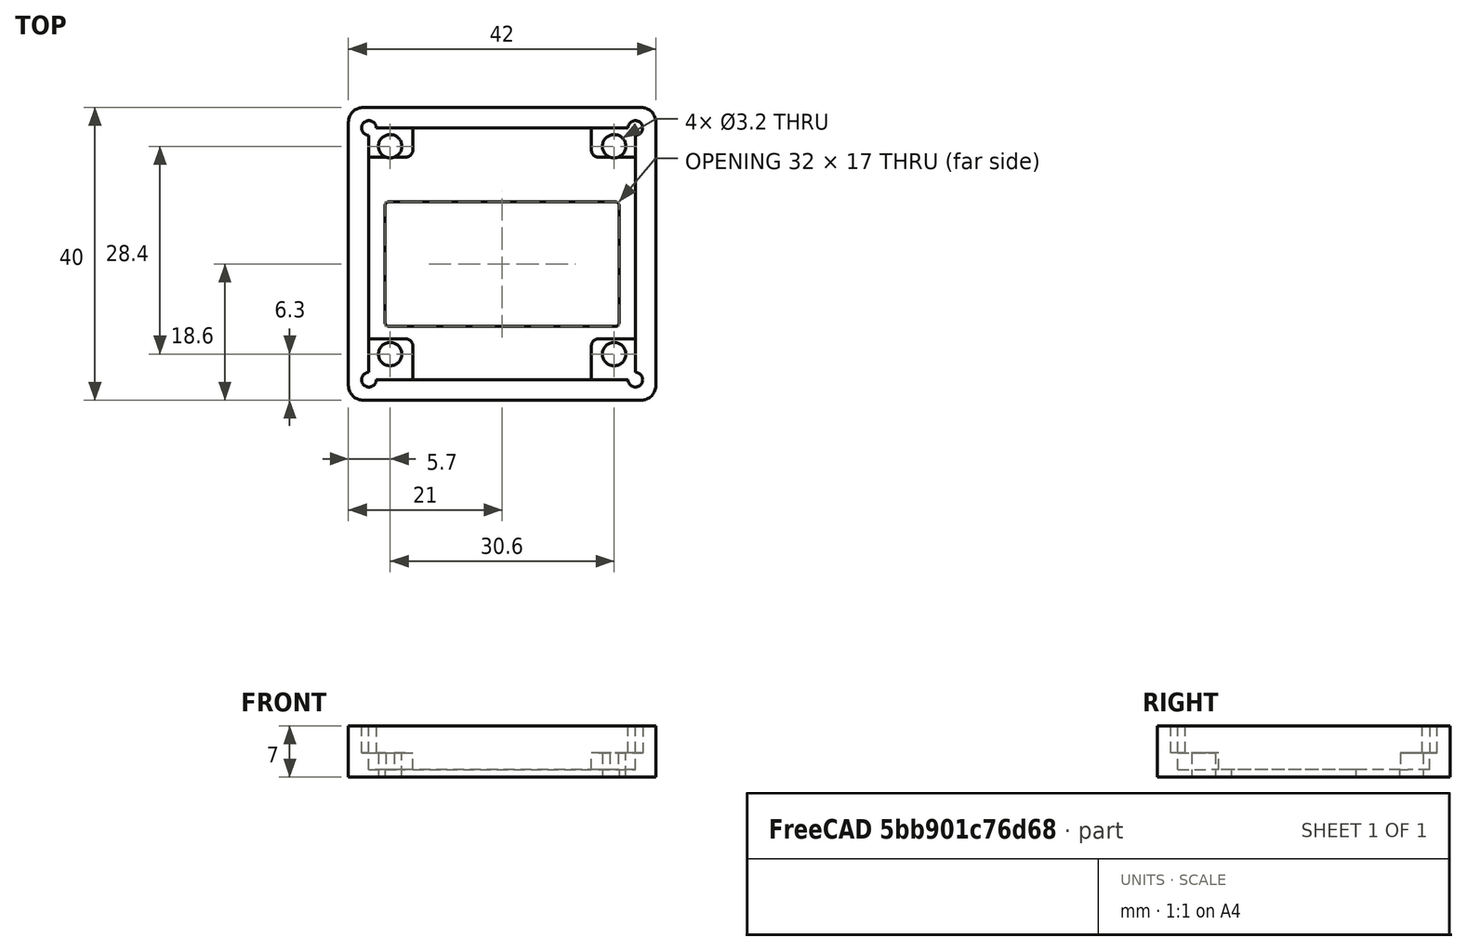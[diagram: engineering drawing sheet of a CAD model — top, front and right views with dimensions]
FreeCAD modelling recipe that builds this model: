
FCSTD DOCUMENT  (FreeCAD 0.18R16131 (Git))
Label: Rahmen_OLED_13
License: All rights reserved
LicenseURL: http://en.wikipedia.org/wiki/All_rights_reserved
objects: Sketcher::SketchObject×6, PartDesign::Pocket×4, PartDesign::Fillet×3, PartDesign::Pad×2, Spreadsheet::Sheet×1, PartDesign::Body×1, Mesh::Feature×1
note: 22 computed .brp shape members not serialized (recipe doc carries the construction recipe); baked Part::Feature solids carry a one-line shape summary decoded from their .brp

FEATURE [Sketcher::SketchObject] Sketch
  MapMode = 5
  Support = -> [XY_Plane]
  expr: Constraints[11] = Constraints.Laenge / 2
  expr: Constraints[10] = Constraints.Breite / 2
  expr: Constraints.Laenge = Measures.A2
  expr: Constraints.Breite = Measures.B2
  sketch-geometry (4):
    g0: LineSegment StartX=-21 StartY=20 StartZ=0 EndX=21 EndY=20 EndZ=0
    g1: LineSegment StartX=21 StartY=20 StartZ=0 EndX=21 EndY=-20 EndZ=0
    g2: LineSegment StartX=21 StartY=-20 StartZ=0 EndX=-21 EndY=-20 EndZ=0
    g3: LineSegment StartX=-21 StartY=-20 StartZ=0 EndX=-21 EndY=20 EndZ=0
  constraints (12):
    c: Coincident(g0,g1)
    c: Coincident(g1,g2)
    c: Coincident(g2,g3)
    c: Coincident(g3,g0)
    c: Horizontal(g0)
    c: Horizontal(g2)
    c: Vertical(g1)
    c: Vertical(g3)
    c: DistanceX(g2,g2) = 42  'Laenge'
    c: DistanceY(g3,g3) = 40  'Breite'
    c: Distance(g-1,g2) = 20
    c: Distance(g-1,g3) = 21
FEATURE [Spreadsheet::Sheet] Spreadsheet  label="Measures"
  cells = A1=Laenge; B1=Breite; C1=Hoehe; D1=OLED_Laenge; E1=OLED_Breite; F1=OLED_Tiefe; A2=42; B2=40; C2=7; D2=36.4; E2=34.4; F2=6
FEATURE [PartDesign::Pad] Pad
  Length = 7
  Length2 = 100
  Profile = -> Sketch
  Type = 0
  expr: Length = Measures.C2
FEATURE [Sketcher::SketchObject] Sketch001
  MapMode = 5
  Placement = pos=(0,0,7) rot=(0,0,1;0rad)
  Support = -> [Pad]
  expr: Constraints[11] = Constraints.OLED_Laenge / 2
  expr: Constraints[10] = Constraints.OLED_Breite / 2
  expr: Constraints.OLED_Laenge = Measures.D2
  expr: Constraints.OLED_Breite = Measures.E2
  sketch-geometry (4):
    g0: LineSegment StartX=-18.2 StartY=17.2 StartZ=0 EndX=18.2 EndY=17.2 EndZ=0
    g1: LineSegment StartX=18.2 StartY=17.2 StartZ=0 EndX=18.2 EndY=-17.2 EndZ=0
    g2: LineSegment StartX=18.2 StartY=-17.2 StartZ=0 EndX=-18.2 EndY=-17.2 EndZ=0
    g3: LineSegment StartX=-18.2 StartY=-17.2 StartZ=0 EndX=-18.2 EndY=17.2 EndZ=0
  constraints (12):
    c: Coincident(g0,g1)
    c: Coincident(g1,g2)
    c: Coincident(g2,g3)
    c: Coincident(g3,g0)
    c: Horizontal(g0)
    c: Horizontal(g2)
    c: Vertical(g1)
    c: Vertical(g3)
    c: DistanceY(g3,g3) = 34.4  'OLED_Breite'
    c: Distance(g2) = 36.4  'OLED_Laenge'
    c: Distance(g-1,g2) = 17.2
    c: Distance(g-1,g3) = 18.2
FEATURE [PartDesign::Pocket] Pocket
  BaseFeature = -> Pad
  Length = 6
  Length2 = 100
  Profile = -> Sketch001
  Type = 0
  expr: Length = Measures.F2
FEATURE [Sketcher::SketchObject] Sketch003
  MapMode = 5
  Placement = pos=(0,0,1) rot=(0,0,1;0rad)
  Support = -> [Pocket]
  sketch-geometry (4):
    g0: LineSegment StartX=-16 StartY=7.1 StartZ=0 EndX=16 EndY=7.1 EndZ=0
    g1: LineSegment StartX=16 StartY=7.1 StartZ=0 EndX=16 EndY=-9.9 EndZ=0
    g2: LineSegment StartX=16 StartY=-9.9 StartZ=0 EndX=-16 EndY=-9.9 EndZ=0
    g3: LineSegment StartX=-16 StartY=-9.9 StartZ=0 EndX=-16 EndY=7.1 EndZ=0
FEATURE [PartDesign::Pocket] Pocket001
  BaseFeature = -> Pocket
  Length = 5
  Length2 = 100
  Profile = -> Sketch003
  Type = 1
FEATURE [Sketcher::SketchObject] Sketch004
  MapMode = 5
  Placement = pos=(0,0,1) rot=(0,0,1;0rad)
  Support = -> [Pocket001]
  sketch-geometry (16):
    g0: LineSegment StartX=-12.2 StartY=13.2 StartZ=0 EndX=-18.2 EndY=13.2 EndZ=0
    g1: LineSegment StartX=-18.2 StartY=13.2 StartZ=0 EndX=-18.2 EndY=17.2 EndZ=0
    g2: LineSegment StartX=-18.2 StartY=17.2 StartZ=0 EndX=-12.2 EndY=17.2 EndZ=0
    g3: LineSegment StartX=-12.2 StartY=17.2 StartZ=0 EndX=-12.2 EndY=13.2 EndZ=0
    g4: LineSegment StartX=12.2 StartY=17.2 StartZ=0 EndX=18.2 EndY=17.2 EndZ=0
    g5: LineSegment StartX=18.2 StartY=17.2 StartZ=0 EndX=18.2 EndY=13.2 EndZ=0
    g6: LineSegment StartX=18.2 StartY=13.2 StartZ=0 EndX=12.2 EndY=13.2 EndZ=0
    g7: LineSegment StartX=12.2 StartY=13.2 StartZ=0 EndX=12.2 EndY=17.2 EndZ=0
    g8: LineSegment StartX=12.2 StartY=-11.6 StartZ=0 EndX=18.2 EndY=-11.6 EndZ=0
    g9: LineSegment StartX=18.2 StartY=-11.6 StartZ=0 EndX=18.2 EndY=-17.2 EndZ=0
    g10: LineSegment StartX=18.2 StartY=-17.2 StartZ=0 EndX=12.2 EndY=-17.2 EndZ=0
    g11: LineSegment StartX=12.2 StartY=-17.2 StartZ=0 EndX=12.2 EndY=-11.6 EndZ=0
    g12: LineSegment StartX=-18.2 StartY=-11.6 StartZ=0 EndX=-12.2 EndY=-11.6 EndZ=0
    g13: LineSegment StartX=-12.2 StartY=-11.6 StartZ=0 EndX=-12.2 EndY=-17.2 EndZ=0
    g14: LineSegment StartX=-12.2 StartY=-17.2 StartZ=0 EndX=-18.2 EndY=-17.2 EndZ=0
    g15: LineSegment StartX=-18.2 StartY=-17.2 StartZ=0 EndX=-18.2 EndY=-11.6 EndZ=0
  constraints (40):
    c: Coincident(g0,g1)
    c: Coincident(g1,g2)
    c: Coincident(g2,g3)
    c: Coincident(g3,g0)
    c: Horizontal(g0)
    c: Horizontal(g2)
    c: Vertical(g1)
    c: Vertical(g3)
    c: DistanceX(g0,g0) = 6
    c: DistanceY(g3,g3) = 4
    c: Coincident(g4,g5)
    c: Coincident(g5,g6)
    c: Coincident(g6,g7)
    c: Coincident(g7,g4)
    c: Horizontal(g4)
    c: Horizontal(g6)
    c: Vertical(g5)
    c: Vertical(g7)
    c: DistanceX(g6,g6) = 6
    c: DistanceY(g7,g7) = 4
    c: Coincident(g8,g9)
    c: Coincident(g9,g10)
    c: Coincident(g10,g11)
    c: Coincident(g11,g8)
    c: Horizontal(g8)
    c: Horizontal(g10)
    c: Vertical(g9)
    c: Vertical(g11)
    c: DistanceX(g8,g8) = 6
    c: DistanceY(g11,g11) = 5.6
    c: Coincident(g12,g13)
    c: Coincident(g13,g14)
    c: Coincident(g14,g15)
    c: Coincident(g15,g12)
    c: Horizontal(g12)
    c: Horizontal(g14)
    c: Vertical(g13)
    c: Vertical(g15)
    c: DistanceY(g13,g13) = 5.6
    c: DistanceX(g12,g12) = 6
FEATURE [PartDesign::Pad] Pad001
  BaseFeature = -> Pocket001
  Length = 2.3
  Length2 = 100
  Profile = -> Sketch004
  Type = 0
FEATURE [Sketcher::SketchObject] Sketch005
  ExternalGeometry = -> [Pad001]
  MapMode = 5
  Placement = pos=(0,0,0) rot=(1,0,0;3.14159rad)
  Support = -> [Pad001]
  sketch-geometry (4):
    g0: Circle CenterX=15.3 CenterY=13.7 CenterZ=0 NormalX=0 NormalY=0 NormalZ=1 AngleXU=0 Radius=1.6
    g1: Circle CenterX=-15.3 CenterY=13.7 CenterZ=0 NormalX=0 NormalY=0 NormalZ=1 AngleXU=0 Radius=1.6
    g2: Circle CenterX=-15.3 CenterY=-14.7 CenterZ=0 NormalX=0 NormalY=0 NormalZ=1 AngleXU=0 Radius=1.6
    g3: Circle CenterX=15.3 CenterY=-14.7 CenterZ=0 NormalX=0 NormalY=0 NormalZ=1 AngleXU=0 Radius=1.6
  constraints (12):
    c: Radius(g0) = 1.6
    c: Equal(g0,g3)
    c: Equal(g0,g2)
    c: Equal(g0,g1)
    c: Distance(g1,g-5) = 6.3
    c: Distance(g0,g-5) = 6.3
    c: Distance(g3,g-5) = 34.7
    c: Distance(g2,g-5) = 34.7
    c: Distance(g3,g-4) = 5.7
    c: Distance(g0,g-4) = 5.7
    c: Distance(g1,g-3) = 5.7
    c: Distance(g2,g-3) = 5.7
FEATURE [PartDesign::Pocket] Pocket002
  BaseFeature = -> Pad001
  Length = 5
  Length2 = 100
  Profile = -> Sketch005
  Type = 1
FEATURE [Sketcher::SketchObject] Sketch006
  ExternalGeometry = -> [Pocket002]
  MapMode = 5
  Placement = pos=(0,0,7) rot=(0,0,1;0rad)
  Support = -> [Pocket002]
  sketch-geometry (4):
    g0: Circle CenterX=18.2 CenterY=17.2 CenterZ=0 NormalX=0 NormalY=0 NormalZ=1 AngleXU=0 Radius=1
    g1: Circle CenterX=-18.2 CenterY=17.2 CenterZ=0 NormalX=0 NormalY=0 NormalZ=1 AngleXU=0 Radius=1
    g2: Circle CenterX=-18.2 CenterY=-17.2 CenterZ=0 NormalX=0 NormalY=0 NormalZ=1 AngleXU=0 Radius=1
    g3: Circle CenterX=18.2 CenterY=-17.2 CenterZ=0 NormalX=0 NormalY=0 NormalZ=1 AngleXU=0 Radius=1
  constraints (8):
    c: Coincident(g0,g-3)
    c: Coincident(g1,g-4)
    c: Coincident(g2,g-4)
    c: Coincident(g3,g-3)
    c: Radius(g1) = 1
    c: Equal(g1,g0)
    c: Equal(g1,g3)
    c: Equal(g1,g2)
FEATURE [PartDesign::Pocket] Pocket003
  BaseFeature = -> Pocket002
  Length = 3.7
  Length2 = 100
  Profile = -> Sketch006
  Type = 0
FEATURE [PartDesign::Fillet] Fillet
  Base = -> Pocket003 [Edge122,Edge113,Edge99,Edge119]
  BaseFeature = -> Pocket003
  Radius = 1
FEATURE [PartDesign::Fillet] Fillet001
  Base = -> Fillet [Edge122,Edge121,Edge124,Edge123]
  BaseFeature = -> Fillet
  Radius = 0.5
FEATURE [PartDesign::Fillet] Fillet002
  Base = -> Fillet001 [Edge138,Edge140,Edge139,Edge137]
  BaseFeature = -> Fillet001
  Radius = 2
FEATURE [PartDesign::Body] Body
  Group = -> [Sketch,Pad,Sketch001,Pocket,Sketch003,Sketch004,Pocket001,Pad001,Sketch005,Pocket002,Sketch006,Pocket003,Fillet,Fillet001,Fillet002]
  Origin = -> Origin
  Tip = -> Fillet002
FEATURE [Mesh::Feature] Mesh  label="Rahmen_OLED_13"
